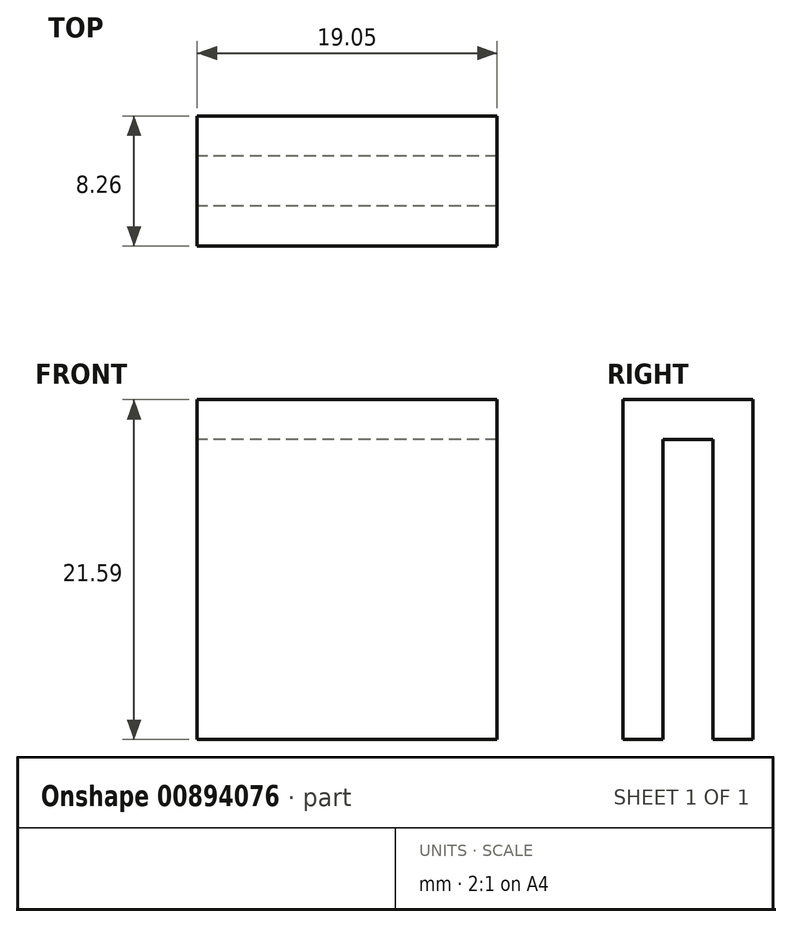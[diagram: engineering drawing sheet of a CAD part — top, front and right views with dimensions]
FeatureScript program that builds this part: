
annotation { "Feature Type Name" : "Feature", "Feature Type Description" : "" }
export const myFeature = defineFeature(function(context is Context, id is Id, definition is map)
    precondition{}
    {
        {
            var Q0;
            Q0=qCreatedBy(makeId("Right.planeOp"),FACE);
            var sketch = newSketch(context, id + "F0", { "sketchPlane" : qUnion([Q0])});
            skLineSegment(sketch, "E0.bottom", {"start": v(-4.13, 21.59) * mm, "end": v(4.13, 21.59) * mm});
            skLineSegment(sketch, "E0.top", {"start": v(-4.13, 0) * mm, "end": v(-1.59, 0) * mm});
            skLineSegment(sketch, "E0.left", {"start": v(-4.13, 21.59) * mm, "end": v(-4.13, 0) * mm});
            skLineSegment(sketch, "E0.right", {"start": v(4.13, 21.59) * mm, "end": v(4.13, 0) * mm});
            skLineSegment(sketch, "E1.top", {"start": v(1.59, 19.05) * mm, "end": v(-1.59, 19.05) * mm});
            skLineSegment(sketch, "E1.left", {"start": v(1.59, 0) * mm, "end": v(1.59, 19.05) * mm});
            skLineSegment(sketch, "E1.right", {"start": v(-1.59, 0) * mm, "end": v(-1.59, 19.05) * mm});
            skPoint(sketch, "E2", {"position": v(0, 19.05) * mm});
            skPoint(sketch, "E3", {"position": v(0, 21.59) * mm});
            skLineSegment(sketch, "E4.trimOffspring", {"start": v(1.59, 0) * mm, "end": v(4.13, 0) * mm});
            skSolve(sketch);
        }
        {
            var Q0;
            Q0 = qSketchRegion(id + "F0", true);
            extrude(context, id + "F1", {"entities" : qUnion([Q0]), "depth" : 19.05 * mm, "offsetDistance" : 25.4 * mm});
        }
    });
